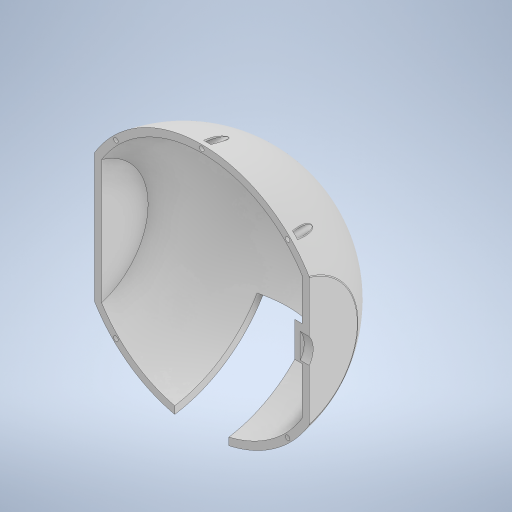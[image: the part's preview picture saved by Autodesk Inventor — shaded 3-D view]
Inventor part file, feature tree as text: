
AUTODESK INVENTOR PART (.ipt)
format: ipt  version: 2023.1 (Build 271208000, 208)  size: 517,120 bytes
history: native  units: mm
features: sketch x8, extrude x7, other x3, fillet x2, projected_geometry x2, revolve x1, shell x1
ambient origin geometry x8: Origin, YZ Plane, XZ Plane, XY Plane, X Axis, Y Axis, Z Axis, Center Point
bodies: Body1 (feature_tree)
feature tree (24):
  other  "솔리드1"
  sketch  "스케치1"
  revolve  "회전1"
  other  "작업 평면2"
  extrude  "돌출14"  Depth=85.0mm
  shell  "쉘2"  Thickness=56.0mm
  extrude  "돌출15"  Depth=17.0mm
  other  "작업 평면3"
  extrude  "돌출16"  Depth=140.0mm
  fillet  "모깎기2"  Radius=4.0mm
  fillet  "모깎기3"  [1 undecoded]
  extrude  "돌출17"  [1 undecoded]
  sketch  "스케치20"
  extrude  "돌출18"  Depth=108.0mm TaperAngle=0.0deg
  extrude  "돌출19"  Depth=4.0mm
  extrude  "돌출20"  Depth=2.5mm
  sketch  "스케치16"
  sketch  "스케치17"
  projected_geometry  "투영된 루프4"
  sketch  "스케치18"
  sketch  "스케치19"
  sketch  "스케치21"
  sketch  "스케치22"
  projected_geometry  "투영된 루프5"
note: 2 required parameter values undecoded (feature->parameter linkage not recoverable at this tier; creation-order binding heuristic only, values carry confidence <= 0.55)
